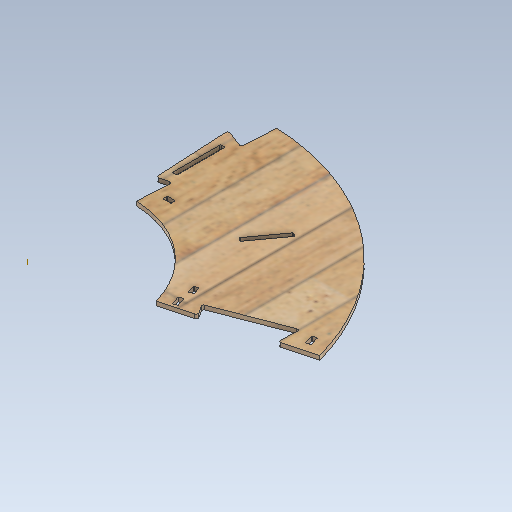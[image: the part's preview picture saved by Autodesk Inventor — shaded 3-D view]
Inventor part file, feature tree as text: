
AUTODESK INVENTOR PART (.ipt)
format: ipt  version: 2020 (Build 240168000, 168)  size: 597,504 bytes
history: native  units: mm
features: extrude x7, sketch x5, mirror x3, pattern_circular x3, plane x1
ambient origin geometry x8: Origin, YZ Plane, XZ Plane, XY Plane, X Axis, Y Axis, Z Axis, Center Point
bodies: Body1 (feature_tree)
feature tree (19):
  extrude  "Extrusion3"  Depth=6.5mm
  extrude  "Extrusion4"  Depth=2.666667mm
  extrude  "Extrusion5"  Depth=1.333333mm
  sketch  "Sketch5"  dims[d25=2.666667mm d32=1.333333mm]
  extrude  "Extrusion7"  TaperAngle=0.0deg  [1 undecoded]
  sketch  "Sketch7"  dims[d40=3.25mm d41=90.0deg d42=3.25mm d43=90.0deg d47=50.0mm d49=360.0deg d52=4.363323mm d54=10.0mm d55=0.0mm d60=0.872665mm d61=12.566371mm d62=13.439035mm d63=2.666667mm d64=0.523599mm d66=0.523599mm d67=2.666667mm d68=2.666667mm d70=12.566371mm d71=12.566371mm d84=300.14mm d85=682.72mm d86=491.43mm d87=150.07mm d88=341.36mm d89=4.363323mm d90=1.919862mm d91=1.919862mm d94=300.14mm d95=682.72mm d96=0.24305mm d104=6.5mm d105=12.0mm d108=1.333333mm d109=1.333333mm d110=1.333333mm d111=1.333333mm d112=0.0mm d113=0.0mm d114=0.0mm d116=1.333333mm d117=1.333333mm d119=1.333333mm d120=1.333333mm d121=6.5mm d122=10.0mm d123=0.0mm d124=0.0mm d126=1.09mm d127=16.333333mm d128=1.333333mm d129=1.333333mm d130=1.333333mm d131=1.333333mm d132=6.5mm d133=10.0mm d135=0.523599mm d137=0.0mm d138=0.0mm d140=0.666667mm d141=3.25mm d142=20.0mm d143=12.566371mm d145=20.0mm d146=12.566371mm d148=0.27mm d149=145.0mm d150=90.0deg d151=90.0deg d152=90.0deg d153=90.0deg d154=20.0mm d155=25.132741mm d157=0.0mm d158=0.0mm]
  extrude  "Extrusion8"  TaperAngle=90.0deg  [1 undecoded]
  extrude  "Extrusion9"  Depth=145.0mm
  plane  "Work Plane1"
  mirror  "Mirror2"
  mirror  "Mirror1"
  pattern_circular  "Circular Pattern1"  Angle=90.0deg  [1 undecoded]
  pattern_circular  "Circular Pattern2"  Count=5 Angle=360.0deg
  pattern_circular  "Circular Pattern3"  [2 undecoded]
  mirror  "Mirror3"
  extrude  "Extrusion10"  Depth=10.0mm TaperAngle=0.0deg
  sketch  "Sketch2"  dims[d15=6.0mm d16=0.0mm d21=6.5mm]
  sketch  "Sketch3"  dims[d23=66.666667mm d24=2.666667mm]
  sketch  "Sketch6"  dims[d33=1.333333mm d38=0.0mm d39=0.0mm]
note: 5 required parameter values undecoded (feature->parameter linkage not recoverable at this tier; creation-order binding heuristic only, values carry confidence <= 0.55)
